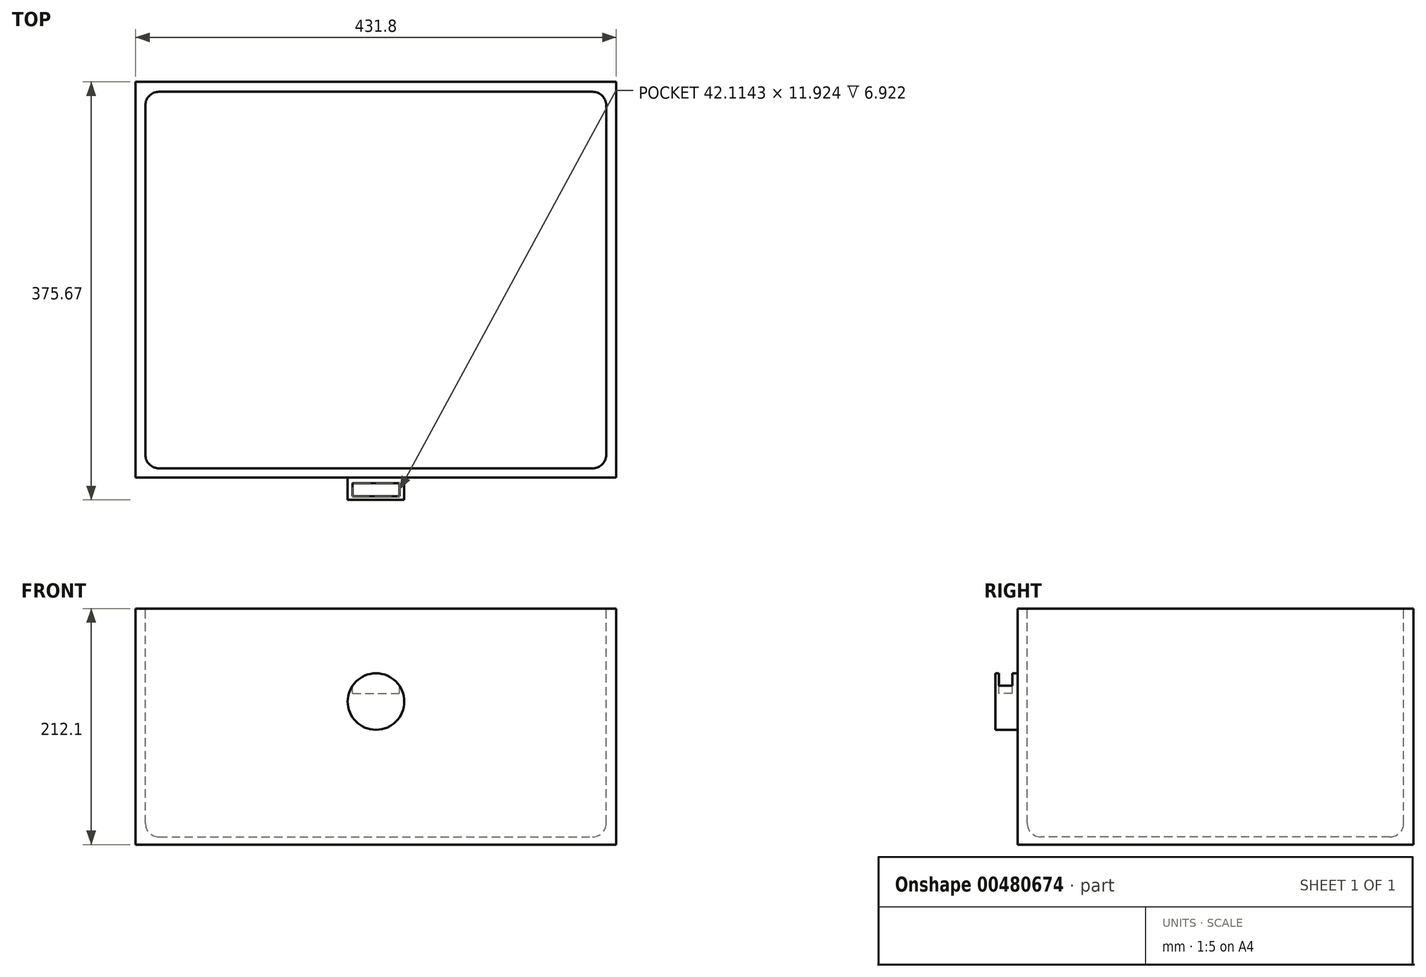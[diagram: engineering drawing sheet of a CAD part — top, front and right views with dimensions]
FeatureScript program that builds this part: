
annotation { "Feature Type Name" : "Feature", "Feature Type Description" : "" }
export const myFeature = defineFeature(function(context is Context, id is Id, definition is map)
    precondition{}
    {
        {
            var Q0;
            Q0=qCreatedBy(makeId("Front.planeOp"),FACE);
            var sketch = newSketch(context, id + "F0", { "sketchPlane" : qUnion([Q0])});
            skLineSegment(sketch, "E0.bottom", {"start": v(-215.9, 106.05) * mm, "end": v(215.9, 106.05) * mm});
            skLineSegment(sketch, "E0.top", {"start": v(-215.9, -106.05) * mm, "end": v(215.9, -106.05) * mm});
            skLineSegment(sketch, "E0.left", {"start": v(-215.9, 106.05) * mm, "end": v(-215.9, -106.05) * mm});
            skLineSegment(sketch, "E0.right", {"start": v(215.9, 106.05) * mm, "end": v(215.9, -106.05) * mm});
            skPoint(sketch, "E0.middle", {"position": v(0, 0) * mm});
            skSolve(sketch);
        }
        {
            var Q0;
            Q0=qSketchRegion(id+"F0",true);
            extrude(context, id + "F1", {"entities" : qUnion([Q0]), "depth" : 355.6 * mm});
        }
        {
            var Q0;
            Q0=makeQuery(id+"F1.opExtrude","SWEPT_FACE",FACE,{"disambiguationData":[OSD([sQuery(id+"F0.wireOp",EDGE,"E0.bottom")])]});
            var sketch = newSketch(context, id + "F2", { "sketchPlane" : qUnion([Q0])});
            skLineSegment(sketch, "E1.bottom", {"start": v(-207.25, -8.91) * mm, "end": v(206.86, -8.91) * mm});
            skLineSegment(sketch, "E1.top", {"start": v(-207.25, -347.2) * mm, "end": v(206.86, -347.2) * mm});
            skLineSegment(sketch, "E1.left", {"start": v(-207.25, -8.91) * mm, "end": v(-207.25, -347.2) * mm});
            skLineSegment(sketch, "E1.right", {"start": v(206.86, -8.91) * mm, "end": v(206.86, -347.2) * mm});
            skSolve(sketch);
        }
        {
            var Q0;
            Q0=qSketchRegion(id+"F2",true);
            extrude(context, id + "F3", {"entities" : qUnion([Q0]), "operationType" : NewBodyOperationType.REMOVE, "oppositeDirection" : true, "depth" : 205.23 * mm});
        }
        {
            var Q0;
            Q0=makeQuery(id+"F1.opExtrude","CAP_FACE",FACE,{"disambiguationData":[OSD([sQuery(id+"F0.wireOp",EDGE,"E0.bottom"),sQuery(id+"F0.wireOp",EDGE,"E0.top"),sQuery(id+"F0.wireOp",EDGE,"E0.left"),sQuery(id+"F0.wireOp",EDGE,"E0.right")])],"isStart":false});
            var sketch = newSketch(context, id + "F4", { "sketchPlane" : qUnion([Q0])});
            skCircle(sketch, "E2", {"center": v(0, 22.44) * mm, "radius": 25.4 * mm});
            skSolve(sketch);
        }
        {
            var Q0;
            Q0=qSketchRegion(id+"F4",true);
            extrude(context, id + "F5", {"entities" : qUnion([Q0]), "operationType" : NewBodyOperationType.ADD, "depth" : 20.07 * mm});
        }
        {
            var Q0;
            Q0=makeQuery(id+"F3.boolean.opBoolean","COPY",EDGE,{"derivedFrom":makeQuery(id+"F3.opExtrude","SWEPT_EDGE",EDGE,{"disambiguationData":[OSD([sQuery(id+"F2.wireOp",EDGE,"E1.top"),sQuery(id+"F2.wireOp",EDGE,"E1.left")])]})});
            var Q1;
            Q1=makeQuery(id+"F3.boolean.opBoolean","COPY",EDGE,{"derivedFrom":makeQuery(id+"F3.opExtrude","CAP_EDGE",EDGE,{"disambiguationData":[OSD([sQuery(id+"F2.wireOp",EDGE,"E1.top")])],"isStart":false})});
            var Q2;
            Q2=makeQuery(id+"F3.boolean.opBoolean","COPY",EDGE,{"derivedFrom":makeQuery(id+"F3.opExtrude","CAP_EDGE",EDGE,{"disambiguationData":[OSD([sQuery(id+"F2.wireOp",EDGE,"E1.left")])],"isStart":false})});
            var Q3;
            Q3=makeQuery(id+"F3.boolean.opBoolean","COPY",EDGE,{"derivedFrom":makeQuery(id+"F3.opExtrude","CAP_EDGE",EDGE,{"disambiguationData":[OSD([sQuery(id+"F2.wireOp",EDGE,"E1.right")])],"isStart":false})});
            var Q4;
            Q4=makeQuery(id+"F3.boolean.opBoolean","COPY",EDGE,{"derivedFrom":makeQuery(id+"F3.opExtrude","SWEPT_EDGE",EDGE,{"disambiguationData":[OSD([sQuery(id+"F2.wireOp",EDGE,"E1.top"),sQuery(id+"F2.wireOp",EDGE,"E1.right")])]})});
            var Q5;
            Q5=makeQuery(id+"F3.boolean.opBoolean","COPY",EDGE,{"derivedFrom":makeQuery(id+"F3.opExtrude","CAP_EDGE",EDGE,{"disambiguationData":[OSD([sQuery(id+"F2.wireOp",EDGE,"E1.bottom")])],"isStart":false})});
            var Q6;
            Q6=makeQuery(id+"F3.boolean.opBoolean","COPY",EDGE,{"derivedFrom":makeQuery(id+"F3.opExtrude","SWEPT_EDGE",EDGE,{"disambiguationData":[OSD([sQuery(id+"F2.wireOp",EDGE,"E1.bottom"),sQuery(id+"F2.wireOp",EDGE,"E1.left")])]})});
            var Q7;
            Q7=makeQuery(id+"F3.boolean.opBoolean","COPY",EDGE,{"derivedFrom":makeQuery(id+"F3.opExtrude","SWEPT_EDGE",EDGE,{"disambiguationData":[OSD([sQuery(id+"F2.wireOp",EDGE,"E1.bottom"),sQuery(id+"F2.wireOp",EDGE,"E1.right")])]})});
            fillet(context, id + "F6", {"entities" : qUnion([Q0, Q1, Q2, Q3, Q4, Q5, Q6, Q7]), "radius" : 12.26 * mm, "tangentPropagation" : true, "allowEdgeOverflow" : false});
        }
        {
            var Q0;
            Q0=makeQuery(id+"F2.imprint","IMPRINT",FACE,{"disambiguationData":[TD([[makeQuery(id+"F2.imprint","IMPRINT",EDGE,{"derivedFrom":sQuery(id+"F2.wireOp",EDGE,"E1.bottom")}),-1.0]])]});
            var sketch = newSketch(context, id + "F7", { "sketchPlane" : qUnion([Q0])});
            skLineSegment(sketch, "E3.bottom", {"start": v(-21.15, -360.56) * mm, "end": v(20.97, -360.56) * mm});
            skLineSegment(sketch, "E3.top", {"start": v(-21.15, -372.49) * mm, "end": v(20.97, -372.49) * mm});
            skLineSegment(sketch, "E3.left", {"start": v(-21.15, -360.56) * mm, "end": v(-21.15, -372.49) * mm});
            skLineSegment(sketch, "E3.right", {"start": v(20.97, -360.56) * mm, "end": v(20.97, -372.49) * mm});
            skSolve(sketch);
        }
        {
            var Q0;
            Q0 = qSketchRegion(id + "F7", true);
            extrude(context, id + "F8", {"entities" : qUnion([Q0]), "operationType" : NewBodyOperationType.REMOVE, "oppositeDirection" : true, "depth" : 76.45 * mm});
        }
    });
